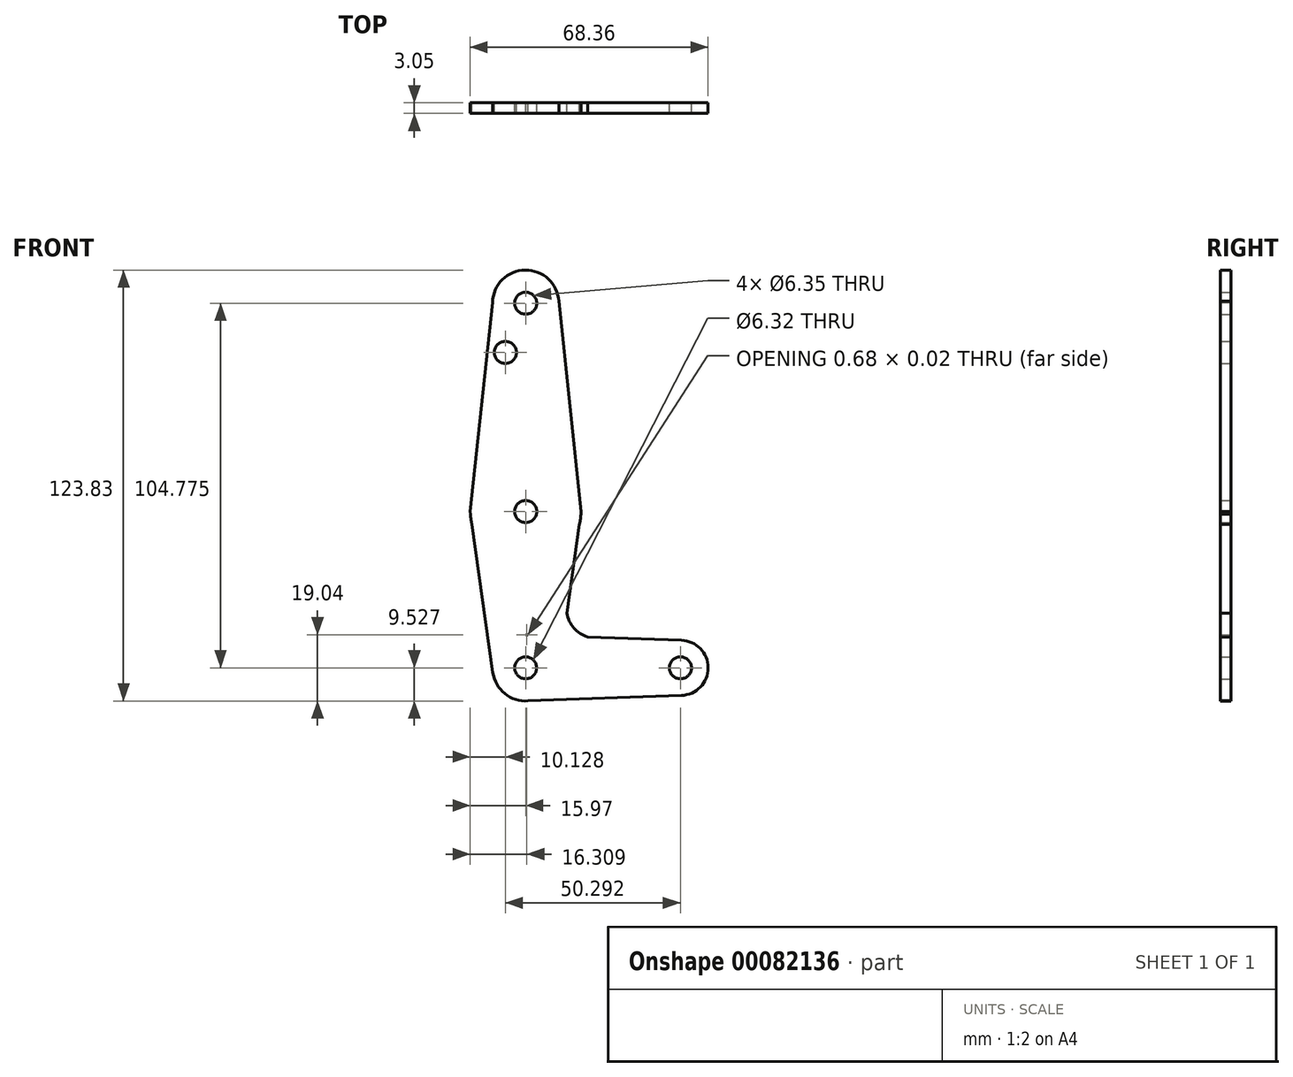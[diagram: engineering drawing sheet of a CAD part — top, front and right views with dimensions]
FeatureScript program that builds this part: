
annotation { "Feature Type Name" : "Feature", "Feature Type Description" : "" }
export const myFeature = defineFeature(function(context is Context, id is Id, definition is map)
    precondition{}
    {
        {
            var Q0;
            Q0=qCreatedBy(makeId("Front.planeOp"),FACE);
            var sketch = newSketch(context, id + "F0", { "sketchPlane" : qUnion([Q0])});
            skLineSegment(sketch, "E0", {"start": v(0, 59.86) * mm, "end": v(0, -44.91) * mm});
            skLineSegment(sketch, "E1", {"start": v(0, -44.91) * mm, "end": v(44.45, -44.91) * mm});
            skCircle(sketch, "E2", {"center": v(0, 59.86) * mm, "radius": 9.53 * mm});
            skArc(sketch, "E3", {"start": v(0.68, -35.41) * mm, "mid": v(-6.97, -51.4) * mm, "end": v(9.53, -44.91) * mm});
            skCircle(sketch, "E4", {"center": v(44.45, -44.91) * mm, "radius": 7.94 * mm});
            skCircle(sketch, "E5", {"center": v(0, 0) * mm, "radius": 15.88 * mm});
            skLineSegment(sketch, "E6", {"start": v(-9.52, 60.1) * mm, "end": v(-15.97, 0) * mm});
            skLineSegment(sketch, "E7", {"start": v(-15.97, 0) * mm, "end": v(-9.43, -46.25) * mm});
            skLineSegment(sketch, "E8", {"start": v(9.51, 60.4) * mm, "end": v(15.97, 0) * mm});
            skLineSegment(sketch, "E9", {"start": v(15.97, 0) * mm, "end": v(11.84, -29.2) * mm});
            skLineSegment(sketch, "E10", {"start": v(0, -54.44) * mm, "end": v(44.73, -52.85) * mm});
            skLineSegment(sketch, "E11", {"start": v(0, -35.39) * mm, "end": v(0.68, -35.41) * mm});
            skArc(sketch, "E12", {"start": v(12.5, -24.55) * mm, "mid": v(12.52, -31.5) * mm, "end": v(17.82, -36.02) * mm});
            skLineSegment(sketch, "E13", {"start": v(0, 59.86) * mm, "end": v(-56.9, 59.86) * mm, "construction": true});
            skLineSegment(sketch, "E14", {"start": v(0, -54.44) * mm, "end": v(-56.66, -54.44) * mm, "construction": true});
            skLineSegment(sketch, "E15", {"start": v(-56.66, -54.44) * mm, "end": v(-56.9, 59.86) * mm, "construction": true});
            skCircle(sketch, "E16", {"center": v(0, 59.86) * mm, "radius": 3.18 * mm});
            skCircle(sketch, "E17", {"center": v(0, 0) * mm, "radius": 3.18 * mm});
            skCircle(sketch, "E18", {"center": v(0, -44.91) * mm, "radius": 3.16 * mm});
            skCircle(sketch, "E19", {"center": v(-5.84, 45.72) * mm, "radius": 3.18 * mm});
            skLineSegment(sketch, "E20", {"start": v(0, 0) * mm, "end": v(0, -44.91) * mm, "construction": true});
            skLineSegment(sketch, "E21", {"start": v(-26.16, -45.21) * mm, "end": v(-26.16, 18.29) * mm, "construction": true});
            skLineSegment(sketch, "E22.trimOffspring", {"start": v(17.82, -36.02) * mm, "end": v(44.73, -36.98) * mm});
            skCircle(sketch, "E23", {"center": v(44.45, -44.91) * mm, "radius": 3.18 * mm});
            skCircle(sketch, "E24", {"center": v(0, -44.91) * mm, "radius": 1.7 * mm});
            skSolve(sketch);
        }
        {
            var Q0;
            Q0 = qSketchRegion(id + "F0", true);
            extrude(context, id + "F1", {"entities" : qUnion([Q0]), "depth" : 3.05 * mm});
        }
    });
